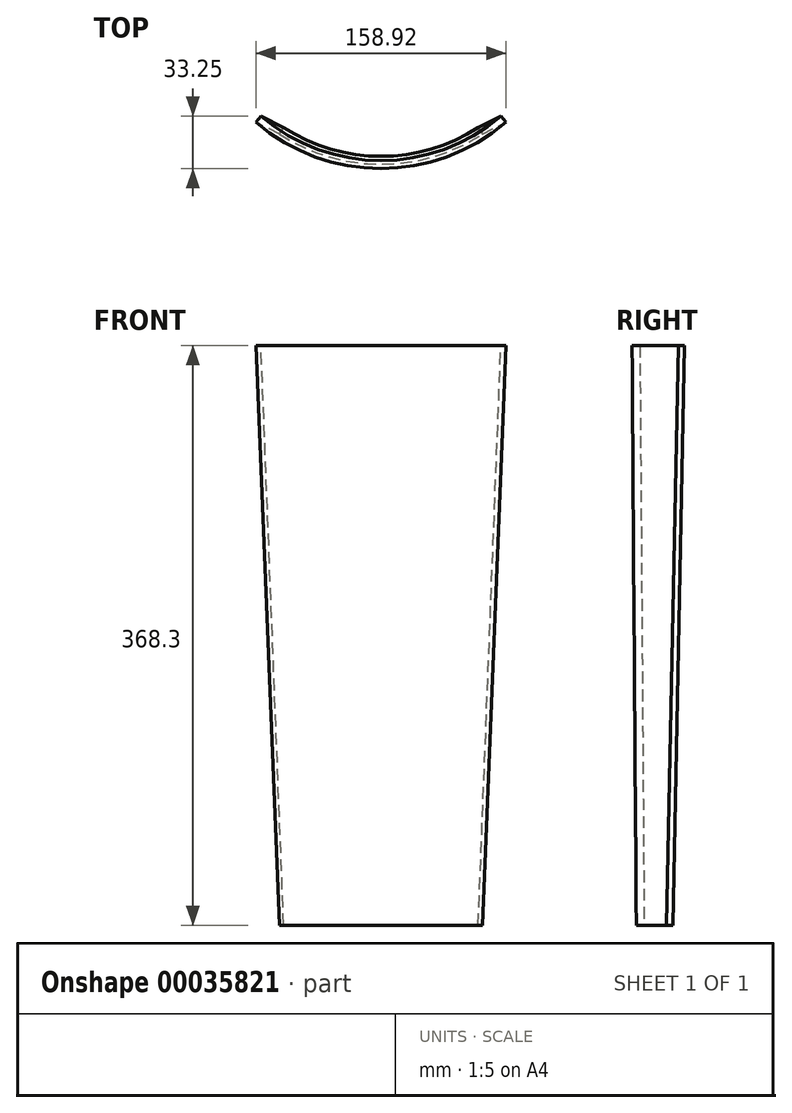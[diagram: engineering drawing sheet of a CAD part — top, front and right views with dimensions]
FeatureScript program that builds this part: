
annotation { "Feature Type Name" : "Feature", "Feature Type Description" : "" }
export const myFeature = defineFeature(function(context is Context, id is Id, definition is map)
    precondition{}
    {
        {
            var Q0;
            Q0=qCreatedBy(makeId("Top.planeOp"),FACE);
            cPlane(context, id + "F0", {"entities" : qUnion([Q0]), "cplaneType" : CPlaneType.OFFSET, "offset" : 368.3 * mm, "oppositeDirection" : true, "width" : 150 * mm, "height" : 150 * mm});
        }
        {
            var Q0;
            Q0=qCreatedBy(makeId("Top.planeOp"),FACE);
            var sketch = newSketch(context, id + "F1", { "sketchPlane" : qUnion([Q0])});
            skArc(sketch, "E0", {"start": v(-76.2, -60.65) * mm, "mid": v(0, -88.9) * mm, "end": v(76.2, -60.65) * mm});
            skLineSegment(sketch, "E1", {"start": v(0, 0) * mm, "end": v(0, -88.9) * mm, "construction": true});
            skArc(sketch, "E2.0", {"start": v(-79.46, -64.44) * mm, "mid": v(0, -93.9) * mm, "end": v(79.46, -64.44) * mm});
            skLineSegment(sketch, "E3", {"start": v(-79.46, -64.44) * mm, "end": v(-76.2, -60.65) * mm});
            skLineSegment(sketch, "E4", {"start": v(76.2, -60.65) * mm, "end": v(79.46, -64.44) * mm});
            skSolve(sketch);
        }
        {
            var Q0;
            Q0=qCreatedBy(id+"F0.planeOp",FACE);
            var sketch = newSketch(context, id + "F2", { "sketchPlane" : qUnion([Q0])});
            skArc(sketch, "E5", {"start": v(-61.78, -67.93) * mm, "mid": v(0, -86.21) * mm, "end": v(61.78, -67.93) * mm});
            skLineSegment(sketch, "E6", {"start": v(0, 0) * mm, "end": v(0, -86.21) * mm, "construction": true});
            skArc(sketch, "E7.0", {"start": v(-64.5, -72.13) * mm, "mid": v(0, -91.21) * mm, "end": v(64.5, -72.13) * mm});
            skLineSegment(sketch, "E8", {"start": v(-64.5, -72.13) * mm, "end": v(-61.78, -67.93) * mm});
            skLineSegment(sketch, "E9", {"start": v(61.78, -67.93) * mm, "end": v(64.5, -72.13) * mm});
            skSolve(sketch);
        }
        {
            var Q0;
            Q0=makeQuery(id+"F2.imprint","IMPRINT",FACE,{"disambiguationData":[TD([[makeQuery(id+"F2.imprint","IMPRINT",EDGE,{"derivedFrom":sQuery(id+"F2.wireOp",EDGE,"E5")}),-1.0]])]});
            var Q1;
            Q1=makeQuery(id+"F1.imprint","IMPRINT",FACE,{"disambiguationData":[TD([[makeQuery(id+"F1.imprint","IMPRINT",EDGE,{"derivedFrom":sQuery(id+"F1.wireOp",EDGE,"E0")}),-1.0]])]});
            loft(context, id + "F3", {"sheetProfilesArray" : [{ "sheetProfileEntities" : qUnion([Q0]) }, { "sheetProfileEntities" : qUnion([Q1]) }]});
        }
    });
